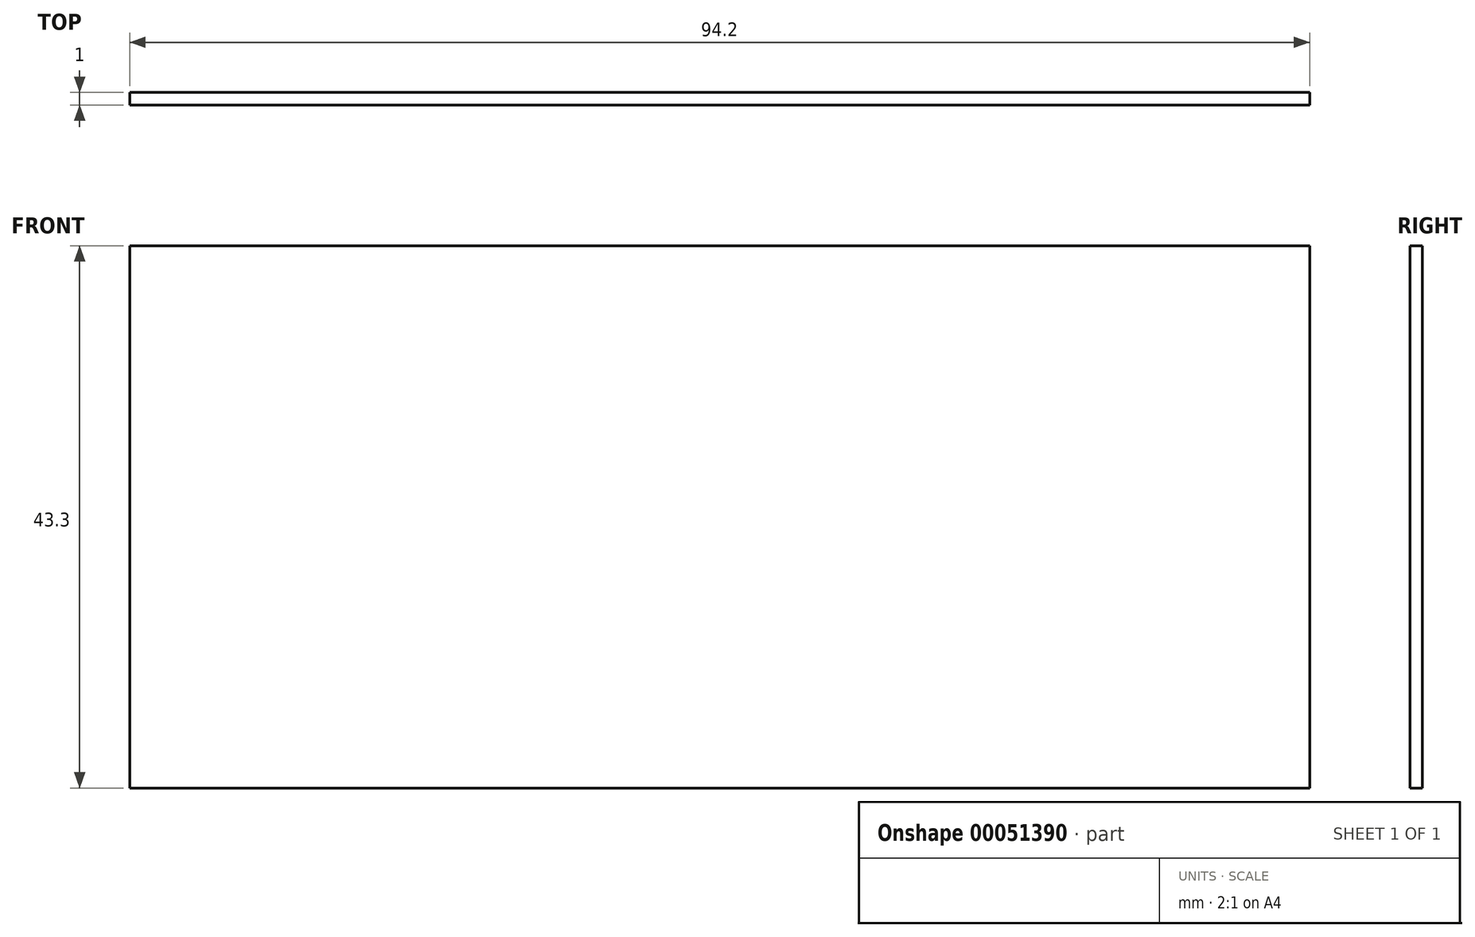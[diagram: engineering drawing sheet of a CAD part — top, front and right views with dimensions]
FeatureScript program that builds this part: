
annotation { "Feature Type Name" : "Feature", "Feature Type Description" : "" }
export const myFeature = defineFeature(function(context is Context, id is Id, definition is map)
    precondition{}
    {
        {
            var Q0;
            Q0=qCreatedBy(makeId("Front.planeOp"),FACE);
            var sketch = newSketch(context, id + "F0", { "sketchPlane" : qUnion([Q0])});
            skLineSegment(sketch, "E0.rect.bottom", {"start": v(47.1, 21.65) * mm, "end": v(-47.1, 21.65) * mm});
            skLineSegment(sketch, "E0.rect.top", {"start": v(47.1, -21.65) * mm, "end": v(-47.1, -21.65) * mm});
            skLineSegment(sketch, "E0.rect.left", {"start": v(47.1, 21.65) * mm, "end": v(47.1, -21.65) * mm});
            skLineSegment(sketch, "E0.rect.right", {"start": v(-47.1, 21.65) * mm, "end": v(-47.1, -21.65) * mm});
            skPoint(sketch, "E0.rect.middle", {"position": v(0, 0) * mm});
            skSolve(sketch);
        }
        {
            var Q0;
            Q0=makeQuery(id+"F0.imprint","IMPRINT",FACE,{"disambiguationData":[TD([[makeQuery(id+"F0.imprint","IMPRINT",EDGE,{"derivedFrom":sQuery(id+"F0.wireOp",EDGE,"E0.rect.bottom")}),1.0]])]});
            extrude(context, id + "F1", {"entities" : qUnion([Q0]), "oppositeDirection" : true, "depth" : 1 * mm});
        }
    });
